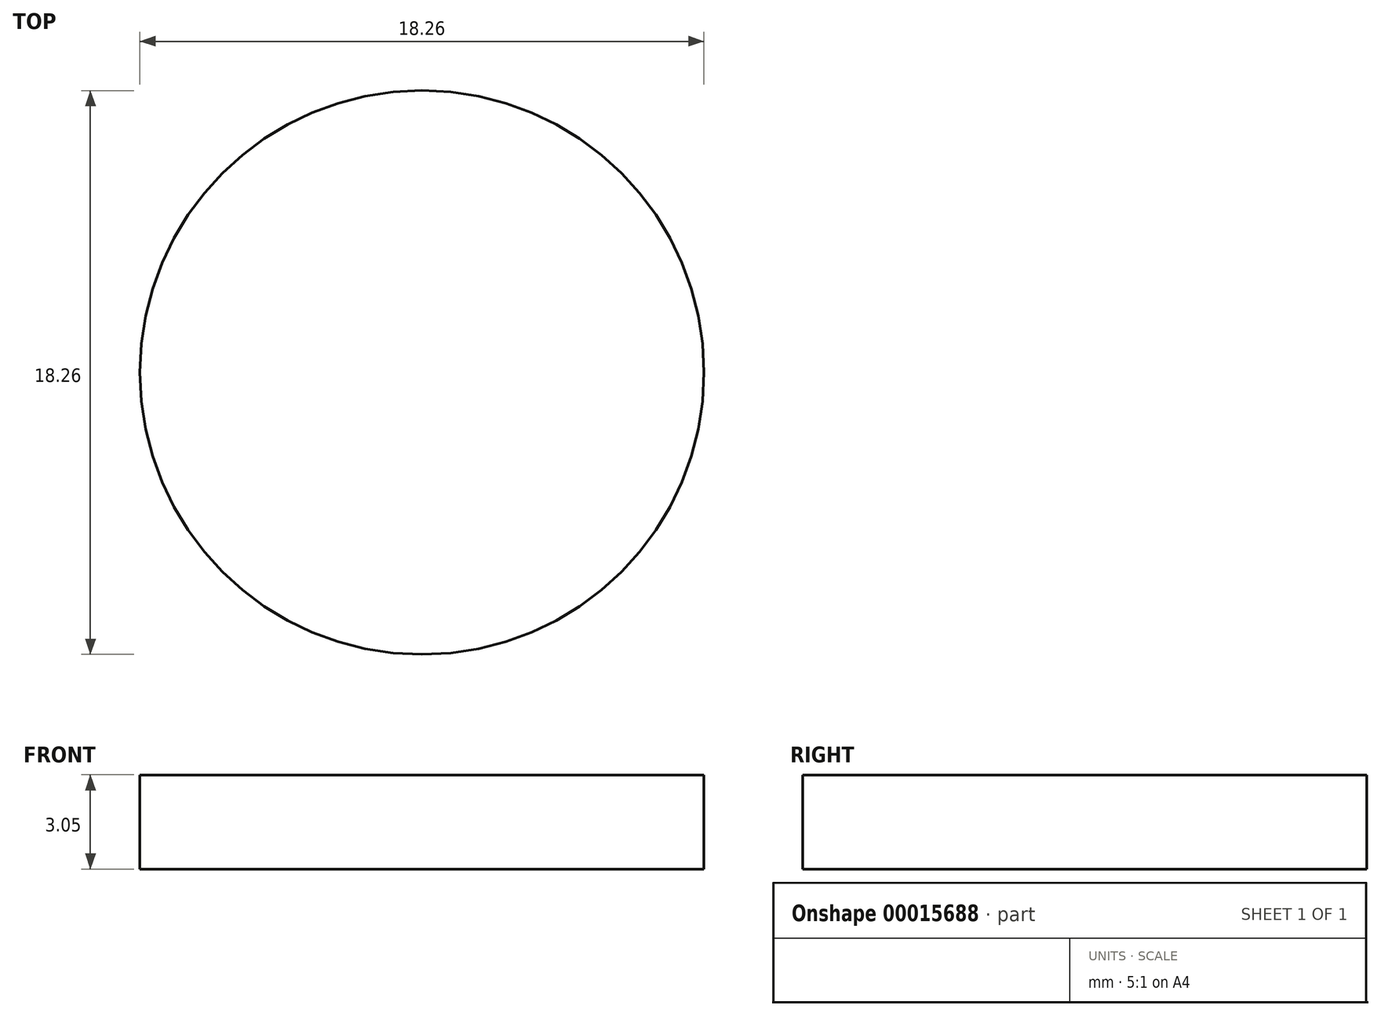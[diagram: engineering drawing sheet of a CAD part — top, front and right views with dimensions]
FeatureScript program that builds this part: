
annotation { "Feature Type Name" : "Feature", "Feature Type Description" : "" }
export const myFeature = defineFeature(function(context is Context, id is Id, definition is map)
    precondition{}
    {
        {
            var Q0;
            Q0=qCreatedBy(makeId("Top.planeOp"),FACE);
            var sketch = newSketch(context, id + "F0", { "sketchPlane" : qUnion([Q0])});
            skCircle(sketch, "E0", {"center": v(0, 0) * mm, "radius": 9.13 * mm});
            skSolve(sketch);
        }
        {
            var Q0;
            Q0 = qSketchRegion(id + "F0", true);
            extrude(context, id + "F1", {"entities" : qUnion([Q0]), "depth" : 3.05 * mm});
        }
    });
